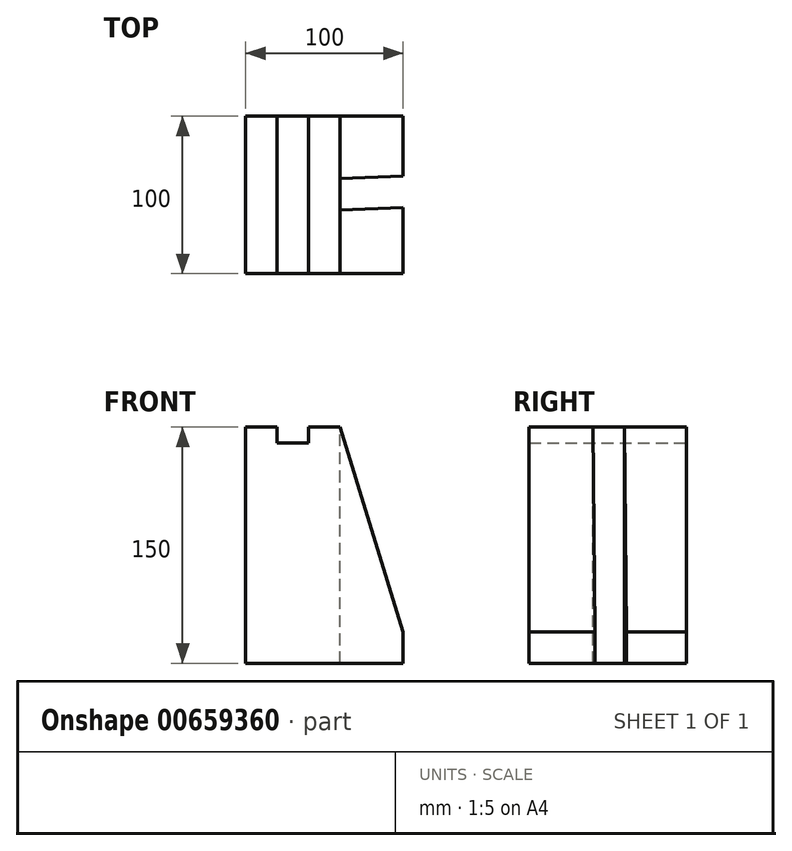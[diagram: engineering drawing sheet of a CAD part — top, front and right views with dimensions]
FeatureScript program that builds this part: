
annotation { "Feature Type Name" : "Feature", "Feature Type Description" : "" }
export const myFeature = defineFeature(function(context is Context, id is Id, definition is map)
    precondition{}
    {
        {
            var Q0;
            Q0=qCreatedBy(makeId("Front.planeOp"),FACE);
            var sketch = newSketch(context, id + "F0", { "sketchPlane" : qUnion([Q0])});
            skLineSegment(sketch, "E0", {"start": v(0, 0) * mm, "end": v(100, 0) * mm});
            skLineSegment(sketch, "E1", {"start": v(0, 0) * mm, "end": v(0, 150) * mm});
            skLineSegment(sketch, "E2", {"start": v(0, 150) * mm, "end": v(20, 150) * mm});
            skLineSegment(sketch, "E3", {"start": v(20, 150) * mm, "end": v(20, 140) * mm});
            skLineSegment(sketch, "E4", {"start": v(20, 140) * mm, "end": v(40, 140) * mm});
            skLineSegment(sketch, "E5", {"start": v(40, 140) * mm, "end": v(40, 150) * mm});
            skLineSegment(sketch, "E6", {"start": v(40, 150) * mm, "end": v(60, 150) * mm});
            skLineSegment(sketch, "E7", {"start": v(100, 0) * mm, "end": v(100, 20) * mm});
            skLineSegment(sketch, "E8", {"start": v(100, 20) * mm, "end": v(60, 150) * mm});
            skSolve(sketch);
        }
        {
            var Q0;
            Q0 = qSketchRegion(id + "F0", true);
            extrude(context, id + "F1", {"entities" : qUnion([Q0]), "depth" : 100 * mm, "offsetDistance" : 25 * mm});
        }
        {
            var Q0;
            Q0=makeQuery(id+"F1.opExtrude","SWEPT_FACE",FACE,{"disambiguationData":[OSD([sQuery(id+"F0.wireOp",EDGE,"E6")])]});
            var sketch = newSketch(context, id + "F2", { "sketchPlane" : qUnion([Q0])});
            skLineSegment(sketch, "E9", {"start": v(48.92, -60.01) * mm, "end": v(48.92, -40.01) * mm});
            skPoint(sketch, "E10.start.orphan", {"position": v(50, -100) * mm});
            skLineSegment(sketch, "E11", {"start": v(48.92, -60.01) * mm, "end": v(148.85, -56.28) * mm});
            skLineSegment(sketch, "E12", {"start": v(148.85, -56.28) * mm, "end": v(148.1, -36.3) * mm});
            skLineSegment(sketch, "E13", {"start": v(148.1, -36.3) * mm, "end": v(48.92, -40.01) * mm});
            skSolve(sketch);
        }
        {
            var Q0;
            {var subQ0=sQuery(id+"F2.wireOp",EDGE,"E12");Q0=makeQuery(id+"F2.imprint","IMPRINT",FACE,{"disambiguationData":[TD([[makeQuery(id+"F2.imprint","IMPRINT",EDGE,{"derivedFrom":subQ0}),1.0]])]});}
            extrude(context, id + "F3", {"entities" : qUnion([Q0]), "operationType" : NewBodyOperationType.REMOVE, "oppositeDirection" : true, "depth" : 150 * mm, "offsetDistance" : 25 * mm});
        }
    });
